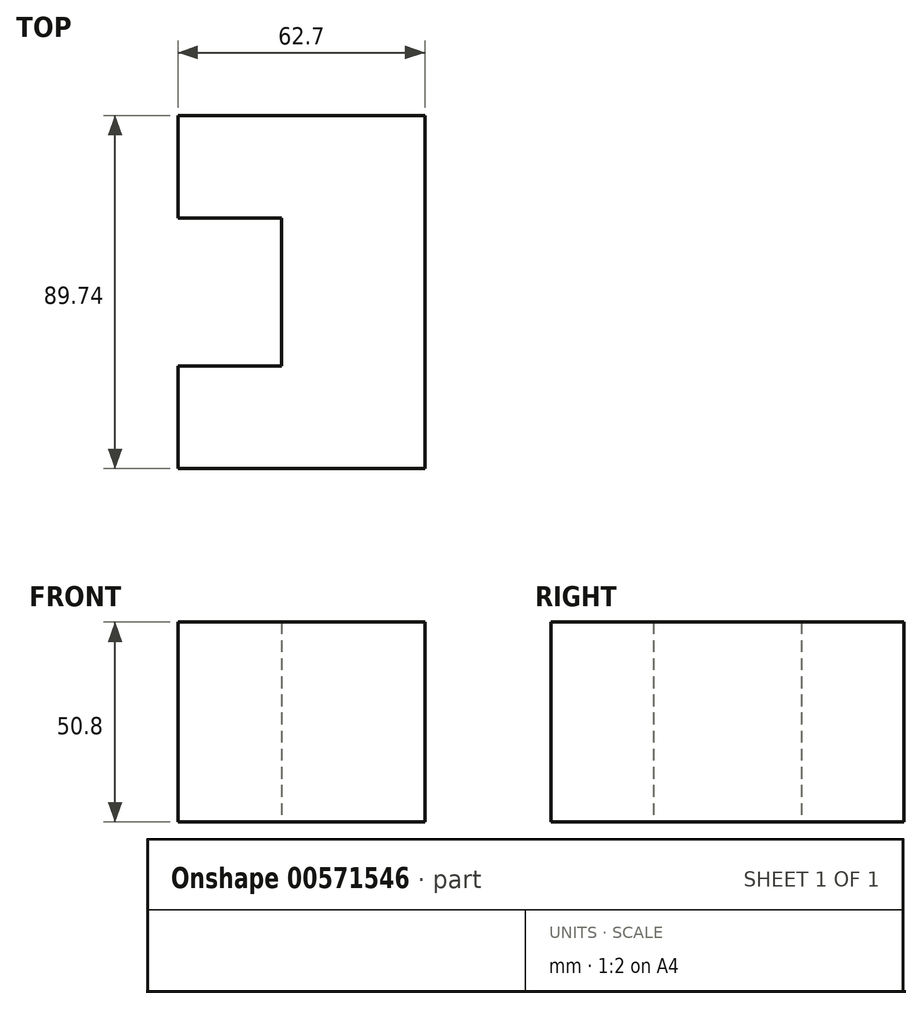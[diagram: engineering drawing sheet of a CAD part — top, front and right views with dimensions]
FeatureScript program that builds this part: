
annotation { "Feature Type Name" : "Feature", "Feature Type Description" : "" }
export const myFeature = defineFeature(function(context is Context, id is Id, definition is map)
    precondition{}
    {
        {
            var Q0;
            Q0=qCreatedBy(makeId("Top.planeOp"),FACE);
            var sketch = newSketch(context, id + "F0", { "sketchPlane" : qUnion([Q0])});
            skLineSegment(sketch, "E0", {"start": v(-34.5, 51.95) * mm, "end": v(-34.5, 25.91) * mm});
            skLineSegment(sketch, "E1", {"start": v(-34.5, 25.91) * mm, "end": v(-8.22, 25.91) * mm});
            skLineSegment(sketch, "E2", {"start": v(-8.22, 25.91) * mm, "end": v(-8.22, -11.76) * mm});
            skLineSegment(sketch, "E3", {"start": v(-8.22, -11.76) * mm, "end": v(-34.5, -11.76) * mm});
            skLineSegment(sketch, "E4", {"start": v(-34.5, -11.76) * mm, "end": v(-34.5, -37.8) * mm});
            skLineSegment(sketch, "E5", {"start": v(-34.5, -37.8) * mm, "end": v(28.2, -37.8) * mm});
            skLineSegment(sketch, "E6", {"start": v(28.2, -37.8) * mm, "end": v(28.2, 51.95) * mm});
            skLineSegment(sketch, "E7", {"start": v(28.2, 51.95) * mm, "end": v(-34.5, 51.95) * mm});
            skSolve(sketch);
        }
        {
            var Q0;
            Q0=makeQuery(id+"F0.imprint","IMPRINT",FACE,{"disambiguationData":[TD([[makeQuery(id+"F0.imprint","IMPRINT",EDGE,{"derivedFrom":sQuery(id+"F0.wireOp",EDGE,"E0")}),1.0]])]});
            extrude(context, id + "F1", {"entities" : qUnion([Q0]), "depth" : 50.8 * mm, "offsetDistance" : 25.4 * mm});
        }
    });
